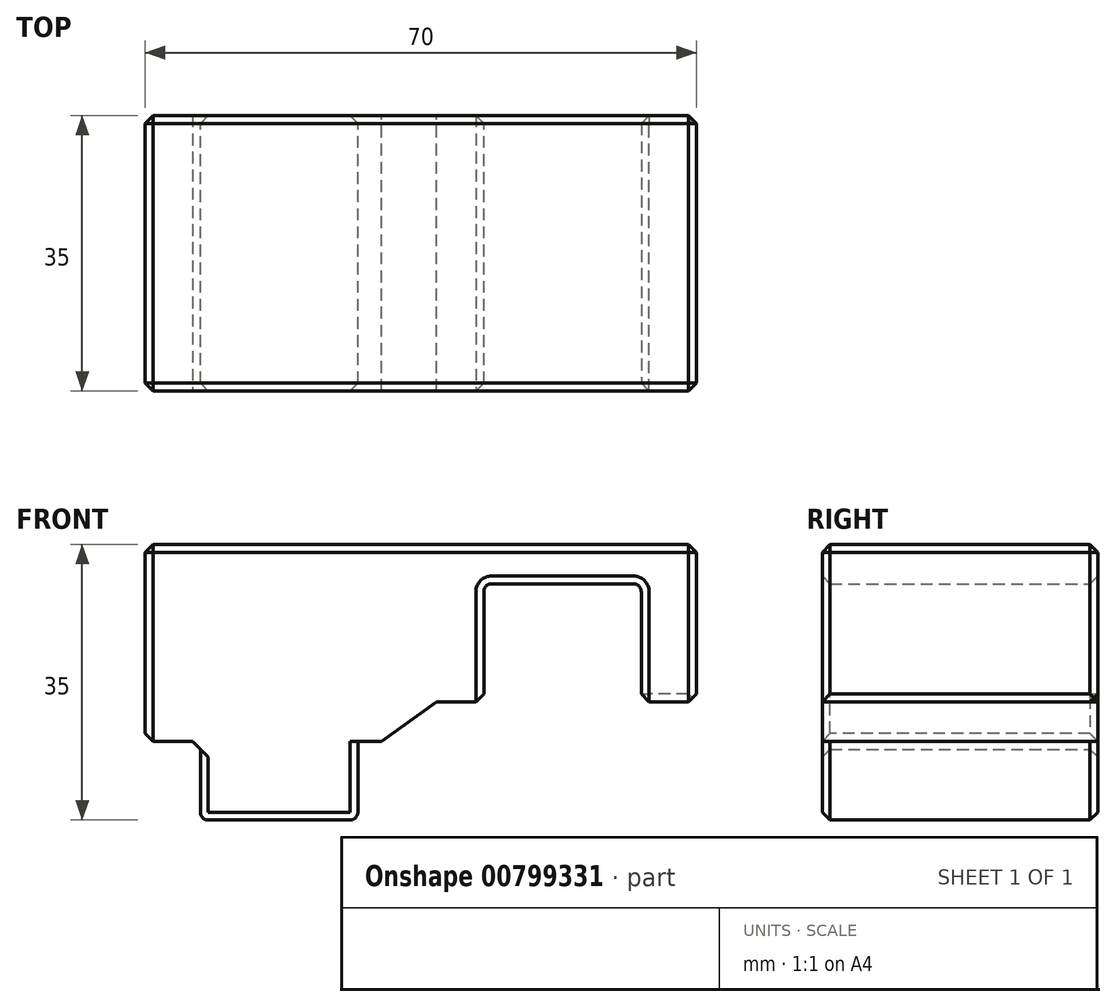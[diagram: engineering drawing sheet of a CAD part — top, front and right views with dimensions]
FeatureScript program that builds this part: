
annotation { "Feature Type Name" : "Feature", "Feature Type Description" : "" }
export const myFeature = defineFeature(function(context is Context, id is Id, definition is map)
    precondition{}
    {
        {
            var Q0;
            Q0=qCreatedBy(makeId("Front.planeOp"),FACE);
            var sketch = newSketch(context, id + "F0", { "sketchPlane" : qUnion([Q0])});
            skLineSegment(sketch, "E0", {"start": v(40.97, 0) * mm, "end": v(33.97, 0) * mm});
            skLineSegment(sketch, "E1", {"start": v(33.97, 0) * mm, "end": v(33.97, 15) * mm});
            skLineSegment(sketch, "E2", {"start": v(33.97, 15) * mm, "end": v(13.97, 15) * mm});
            skLineSegment(sketch, "E3", {"start": v(13.97, 15) * mm, "end": v(13.97, 0) * mm});
            skLineSegment(sketch, "E4", {"start": v(13.97, 0) * mm, "end": v(7.97, 0) * mm});
            skLineSegment(sketch, "E5", {"start": v(7.97, 0) * mm, "end": v(0.99, -5) * mm});
            skLineSegment(sketch, "E6", {"start": v(0.99, -5) * mm, "end": v(-2.03, -5) * mm});
            skLineSegment(sketch, "E7", {"start": v(-2.03, -5) * mm, "end": v(-2.03, -15) * mm});
            skLineSegment(sketch, "E8", {"start": v(-2.03, -15) * mm, "end": v(-22.03, -15) * mm});
            skLineSegment(sketch, "E9", {"start": v(-22.03, -15) * mm, "end": v(-22.03, -5) * mm});
            skLineSegment(sketch, "E10", {"start": v(-22.03, -5) * mm, "end": v(-29.03, -5) * mm});
            skLineSegment(sketch, "E11", {"start": v(-29.03, -5) * mm, "end": v(-29.03, 20) * mm});
            skLineSegment(sketch, "E12", {"start": v(-29.03, 20) * mm, "end": v(40.97, 20) * mm});
            skLineSegment(sketch, "E13", {"start": v(40.97, 20) * mm, "end": v(40.97, 0) * mm});
            skSolve(sketch);
        }
        {
            var Q0;
            Q0=makeQuery(id+"F0.imprint","IMPRINT",FACE,{"disambiguationData":[TD([[makeQuery(id+"F0.imprint","IMPRINT",EDGE,{"derivedFrom":sQuery(id+"F0.wireOp",EDGE,"E0")}),-1.0]])]});
            extrude(context, id + "F1", {"entities" : qUnion([Q0]), "endBound" : BoundingType.SYMMETRIC, "depth" : 35 * mm, "offsetDistance" : 25.4 * mm});
        }
        {
            var Q0;
            Q0=makeQuery(id+"F1.opExtrude","SWEPT_EDGE",EDGE,{"disambiguationData":[OSD([sQuery(id+"F0.wireOp",EDGE,"E0"),sQuery(id+"F0.wireOp",EDGE,"E13")])]});
            var Q1;
            Q1=makeQuery(id+"F1.opExtrude","CAP_EDGE",EDGE,{"disambiguationData":[OSD([sQuery(id+"F0.wireOp",EDGE,"E13")])],"isStart":false});
            var Q2;
            Q2=makeQuery(id+"F1.opExtrude","SWEPT_EDGE",EDGE,{"disambiguationData":[OSD([sQuery(id+"F0.wireOp",EDGE,"E12"),sQuery(id+"F0.wireOp",EDGE,"E13")])]});
            var Q3;
            Q3=makeQuery(id+"F1.opExtrude","CAP_EDGE",EDGE,{"disambiguationData":[OSD([sQuery(id+"F0.wireOp",EDGE,"E13")])],"isStart":true});
            var Q4;
            Q4=makeQuery(id+"F1.opExtrude","CAP_EDGE",EDGE,{"disambiguationData":[OSD([sQuery(id+"F0.wireOp",EDGE,"E12")])],"isStart":false});
            var Q5;
            Q5=makeQuery(id+"F1.opExtrude","CAP_EDGE",EDGE,{"disambiguationData":[OSD([sQuery(id+"F0.wireOp",EDGE,"E12")])],"isStart":true});
            var Q6;
            Q6=makeQuery(id+"F1.opExtrude","SWEPT_EDGE",EDGE,{"disambiguationData":[OSD([sQuery(id+"F0.wireOp",EDGE,"E11"),sQuery(id+"F0.wireOp",EDGE,"E12")])]});
            var Q7;
            Q7=makeQuery(id+"F1.opExtrude","CAP_EDGE",EDGE,{"disambiguationData":[OSD([sQuery(id+"F0.wireOp",EDGE,"E11")])],"isStart":false});
            var Q8;
            Q8=makeQuery(id+"F1.opExtrude","CAP_EDGE",EDGE,{"disambiguationData":[OSD([sQuery(id+"F0.wireOp",EDGE,"E11")])],"isStart":true});
            var Q9;
            Q9=makeQuery(id+"F1.opExtrude","SWEPT_EDGE",EDGE,{"disambiguationData":[OSD([sQuery(id+"F0.wireOp",EDGE,"E10"),sQuery(id+"F0.wireOp",EDGE,"E11")])]});
            var Q10;
            Q10=makeQuery(id+"F1.opExtrude","SWEPT_EDGE",EDGE,{"disambiguationData":[OSD([sQuery(id+"F0.wireOp",EDGE,"E9"),sQuery(id+"F0.wireOp",EDGE,"E10")])]});
            chamfer(context, id + "F2", {"entities" : qUnion([Q0, Q1, Q2, Q3, Q4, Q5, Q6, Q7, Q8, Q9, Q10]), "width" : 1 * mm, "tangentPropagation" : true});
        }
        {
            var Q0;
            Q0=makeQuery(id+"F1.opExtrude","SWEPT_EDGE",EDGE,{"disambiguationData":[OSD([sQuery(id+"F0.wireOp",EDGE,"E8"),sQuery(id+"F0.wireOp",EDGE,"E9")])]});
            var Q1;
            Q1=makeQuery(id+"F1.opExtrude","SWEPT_EDGE",EDGE,{"disambiguationData":[OSD([sQuery(id+"F0.wireOp",EDGE,"E7"),sQuery(id+"F0.wireOp",EDGE,"E8")])]});
            var Q2;
            Q2=makeQuery(id+"F1.opExtrude","SWEPT_EDGE",EDGE,{"disambiguationData":[OSD([sQuery(id+"F0.wireOp",EDGE,"E2"),sQuery(id+"F0.wireOp",EDGE,"E3")])]});
            var Q3;
            Q3=makeQuery(id+"F1.opExtrude","SWEPT_EDGE",EDGE,{"disambiguationData":[OSD([sQuery(id+"F0.wireOp",EDGE,"E1"),sQuery(id+"F0.wireOp",EDGE,"E2")])]});
            fillet(context, id + "F3", {"entities" : qUnion([Q0, Q1, Q2, Q3]), "radius" : 1 * mm, "tangentPropagation" : true, "allowEdgeOverflow" : false});
        }
        {
            var Q0;
            Q0=makeQuery(id+"F1.opExtrude","SWEPT_EDGE",EDGE,{"disambiguationData":[OSD([sQuery(id+"F0.wireOp",EDGE,"E0"),sQuery(id+"F0.wireOp",EDGE,"E1")])]});
            var Q1;
            Q1=makeQuery(id+"F1.opExtrude","CAP_EDGE",EDGE,{"disambiguationData":[OSD([sQuery(id+"F0.wireOp",EDGE,"E0")])],"isStart":true});
            var Q2;
            Q2=makeQuery(id+"F1.opExtrude","SWEPT_EDGE",EDGE,{"disambiguationData":[OSD([sQuery(id+"F0.wireOp",EDGE,"E3"),sQuery(id+"F0.wireOp",EDGE,"E4")])]});
            var Q3;
            Q3=makeQuery(id+"F1.opExtrude","CAP_EDGE",EDGE,{"disambiguationData":[OSD([sQuery(id+"F0.wireOp",EDGE,"E2")])],"isStart":false});
            var Q4;
            Q4=makeQuery(id+"F1.opExtrude","CAP_EDGE",EDGE,{"disambiguationData":[OSD([sQuery(id+"F0.wireOp",EDGE,"E2")])],"isStart":true});
            var Q5;
            Q5=makeQuery(id+"F1.opExtrude","CAP_EDGE",EDGE,{"disambiguationData":[OSD([sQuery(id+"F0.wireOp",EDGE,"E8")])],"isStart":true});
            var Q6;
            Q6=makeQuery(id+"F1.opExtrude","CAP_EDGE",EDGE,{"disambiguationData":[OSD([sQuery(id+"F0.wireOp",EDGE,"E8")])],"isStart":false});
            chamfer(context, id + "F4", {"entities" : qUnion([Q0, Q1, Q2, Q3, Q4, Q5, Q6]), "width" : 1 * mm, "tangentPropagation" : true});
        }
    });
